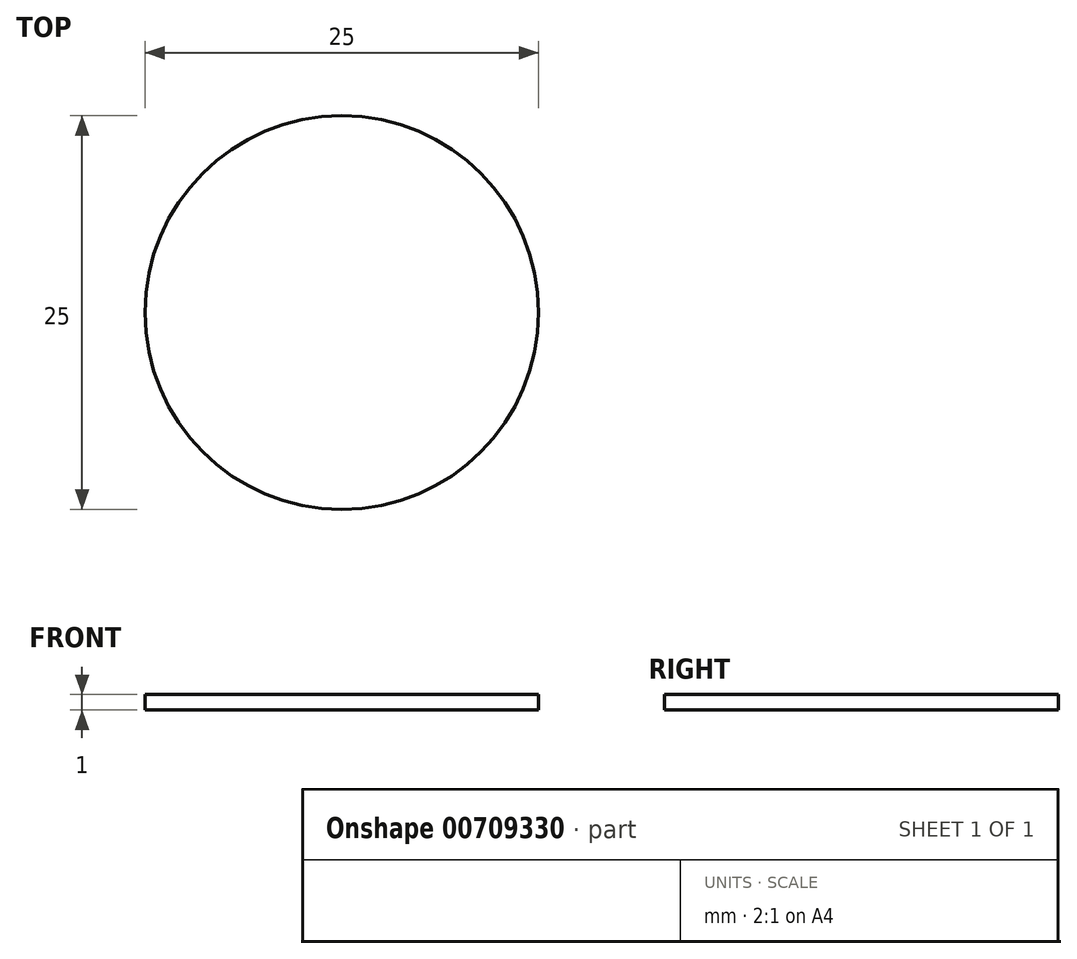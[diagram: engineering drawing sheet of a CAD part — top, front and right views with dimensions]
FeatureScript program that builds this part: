
annotation { "Feature Type Name" : "Feature", "Feature Type Description" : "" }
export const myFeature = defineFeature(function(context is Context, id is Id, definition is map)
    precondition{}
    {
        {
            var Q0;
            Q0=qCreatedBy(makeId("Top.planeOp"),FACE);
            var sketch = newSketch(context, id + "F0", { "sketchPlane" : qUnion([Q0])});
            skCircle(sketch, "E0", {"center": v(0, 0) * mm, "radius": 12.5 * mm});
            skSolve(sketch);
        }
        {
            var Q0;
            Q0 = qSketchRegion(id + "F0", true);
            extrude(context, id + "F1", {"entities" : qUnion([Q0]), "depth" : 1 * mm, "offsetDistance" : 25 * mm});
        }
    });
